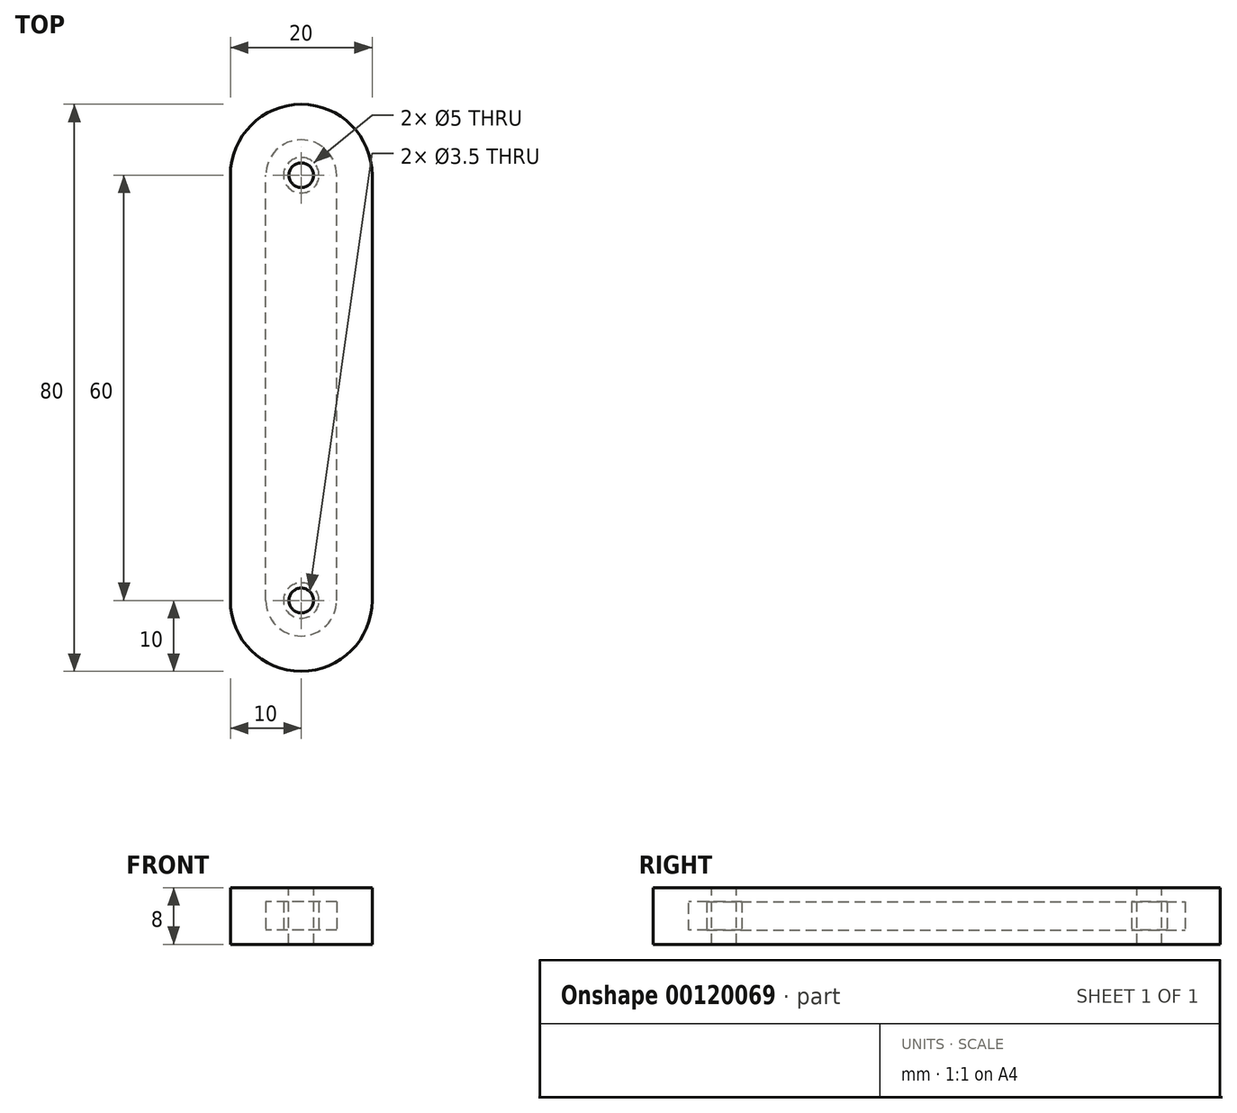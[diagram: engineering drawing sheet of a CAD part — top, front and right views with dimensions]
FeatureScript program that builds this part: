
annotation { "Feature Type Name" : "Feature", "Feature Type Description" : "" }
export const myFeature = defineFeature(function(context is Context, id is Id, definition is map)
    precondition{}
    {
        {
            var Q0;
            Q0=qCreatedBy(makeId("Top.planeOp"),FACE);
            var sketch = newSketch(context, id + "F0", { "sketchPlane" : qUnion([Q0])});
            skLineSegment(sketch, "E0.bottom", {"start": v(10, -40) * mm, "end": v(-10, -40) * mm});
            skLineSegment(sketch, "E0.top", {"start": v(10, 40) * mm, "end": v(-10, 40) * mm});
            skLineSegment(sketch, "E0.left", {"start": v(10, -40) * mm, "end": v(10, 40) * mm});
            skLineSegment(sketch, "E0.right", {"start": v(-10, -40) * mm, "end": v(-10, 40) * mm});
            skPoint(sketch, "E0.middle", {"position": v(0, 0) * mm});
            skSolve(sketch);
        }
        {
            var Q0;
            Q0 = qSketchRegion(id + "F0", true);
            extrude(context, id + "F1", {"entities" : qUnion([Q0]), "endBound" : BoundingType.SYMMETRIC, "depth" : 8 * mm});
        }
        {
            var Q0;
            Q0=qCreatedBy(makeId("Top.planeOp"),FACE);
            var sketch = newSketch(context, id + "F2", { "sketchPlane" : qUnion([Q0])});
            skLineSegment(sketch, "E1.bottom", {"start": v(5, -35) * mm, "end": v(-5, -35) * mm});
            skLineSegment(sketch, "E1.top", {"start": v(5, 35) * mm, "end": v(-5, 35) * mm});
            skLineSegment(sketch, "E1.left", {"start": v(5, -35) * mm, "end": v(5, 35) * mm});
            skLineSegment(sketch, "E1.right", {"start": v(-5, -35) * mm, "end": v(-5, 35) * mm});
            skPoint(sketch, "E1.middle", {"position": v(0, 0) * mm});
            skCircle(sketch, "E2", {"center": v(0, 30) * mm, "radius": 2.5 * mm});
            skCircle(sketch, "E3.MirrorC", {"center": v(0, -30) * mm, "radius": 2.5 * mm});
            skSolve(sketch);
        }
        {
            var Q0;
            Q0 = qSketchRegion(id + "F2", true);
            extrude(context, id + "F3", {"entities" : qUnion([Q0]), "endBound" : BoundingType.SYMMETRIC, "depth" : 4 * mm});
        }
        {
            var Q0;
            Q0=makeQuery(id+"F1.opExtrude","CAP_FACE",FACE,{"disambiguationData":[OSD([sQuery(id+"F0.wireOp",EDGE,"E0.bottom"),sQuery(id+"F0.wireOp",EDGE,"E0.top"),sQuery(id+"F0.wireOp",EDGE,"E0.left"),sQuery(id+"F0.wireOp",EDGE,"E0.right")])],"isStart":false});
            var sketch = newSketch(context, id + "F4", { "sketchPlane" : qUnion([Q0])});
            skCircle(sketch, "E4", {"center": v(0, 30) * mm, "radius": 1.75 * mm});
            skCircle(sketch, "E5", {"center": v(0, -30) * mm, "radius": 1.75 * mm});
            skSolve(sketch);
        }
        {
            var Q0;
            Q0 = qSketchRegion(id + "F4", true);
            extrude(context, id + "F5", {"entities" : qUnion([Q0]), "operationType" : NewBodyOperationType.REMOVE, "endBound" : BoundingType.THROUGH_ALL, "oppositeDirection" : true, "depth" : 25 * mm});
        }
        {
            var Q0;
            Q0=makeQuery(id+"F3.opExtrude","SWEPT_EDGE",EDGE,{"disambiguationData":[OSD([sQuery(id+"F2.wireOp",EDGE,"E1.bottom"),sQuery(id+"F2.wireOp",EDGE,"E1.left")])]});
            var Q1;
            Q1=makeQuery(id+"F3.opExtrude","SWEPT_EDGE",EDGE,{"disambiguationData":[OSD([sQuery(id+"F2.wireOp",EDGE,"E1.bottom"),sQuery(id+"F2.wireOp",EDGE,"E1.right")])]});
            var Q2;
            Q2=makeQuery(id+"F3.opExtrude","SWEPT_EDGE",EDGE,{"disambiguationData":[OSD([sQuery(id+"F2.wireOp",EDGE,"E1.top"),sQuery(id+"F2.wireOp",EDGE,"E1.left")])]});
            var Q3;
            Q3=makeQuery(id+"F3.opExtrude","SWEPT_EDGE",EDGE,{"disambiguationData":[OSD([sQuery(id+"F2.wireOp",EDGE,"E1.top"),sQuery(id+"F2.wireOp",EDGE,"E1.right")])]});
            fillet(context, id + "F6", {"entities" : qUnion([Q0, Q1, Q2, Q3]), "radius" : 5 * mm, "tangentPropagation" : true, "allowEdgeOverflow" : false});
        }
        {
            var Q0;
            Q0=makeQuery(id+"F1.opExtrude","SWEPT_EDGE",EDGE,{"disambiguationData":[OSD([sQuery(id+"F0.wireOp",EDGE,"E0.top"),sQuery(id+"F0.wireOp",EDGE,"E0.left")])]});
            var Q1;
            Q1=makeQuery(id+"F1.opExtrude","SWEPT_EDGE",EDGE,{"disambiguationData":[OSD([sQuery(id+"F0.wireOp",EDGE,"E0.top"),sQuery(id+"F0.wireOp",EDGE,"E0.right")])]});
            var Q2;
            Q2=makeQuery(id+"F1.opExtrude","SWEPT_EDGE",EDGE,{"disambiguationData":[OSD([sQuery(id+"F0.wireOp",EDGE,"E0.bottom"),sQuery(id+"F0.wireOp",EDGE,"E0.right")])]});
            var Q3;
            Q3=makeQuery(id+"F1.opExtrude","SWEPT_EDGE",EDGE,{"disambiguationData":[OSD([sQuery(id+"F0.wireOp",EDGE,"E0.bottom"),sQuery(id+"F0.wireOp",EDGE,"E0.left")])]});
            fillet(context, id + "F7", {"entities" : qUnion([Q0, Q1, Q2, Q3]), "radius" : 10 * mm, "tangentPropagation" : true, "allowEdgeOverflow" : false});
        }
        {
            var Q0;
            Q0=makeQuery(id+"F3.opExtrude","SWEPT_BODY",BODY,{"disambiguationData":[OSD([sQuery(id+"F2.wireOp",EDGE,"E1.bottom"),sQuery(id+"F2.wireOp",EDGE,"E1.top"),sQuery(id+"F2.wireOp",EDGE,"E1.left"),sQuery(id+"F2.wireOp",EDGE,"E1.right"),sQuery(id+"F2.wireOp",EDGE,"E2"),sQuery(id+"F2.wireOp",EDGE,"E3.MirrorC")])]});
            var Q1;
            Q1=makeQuery(id+"F1.opExtrude","SWEPT_BODY",BODY,{"disambiguationData":[OSD([sQuery(id+"F0.wireOp",EDGE,"E0.bottom"),sQuery(id+"F0.wireOp",EDGE,"E0.top"),sQuery(id+"F0.wireOp",EDGE,"E0.left"),sQuery(id+"F0.wireOp",EDGE,"E0.right")])]});
            booleanBodies(context, id + "F8", {"operationType" : BooleanOperationType.SUBTRACTION, "tools" : qUnion([Q0]), "targets" : qUnion([Q1]), "keepTools" : true});
        }
    });
